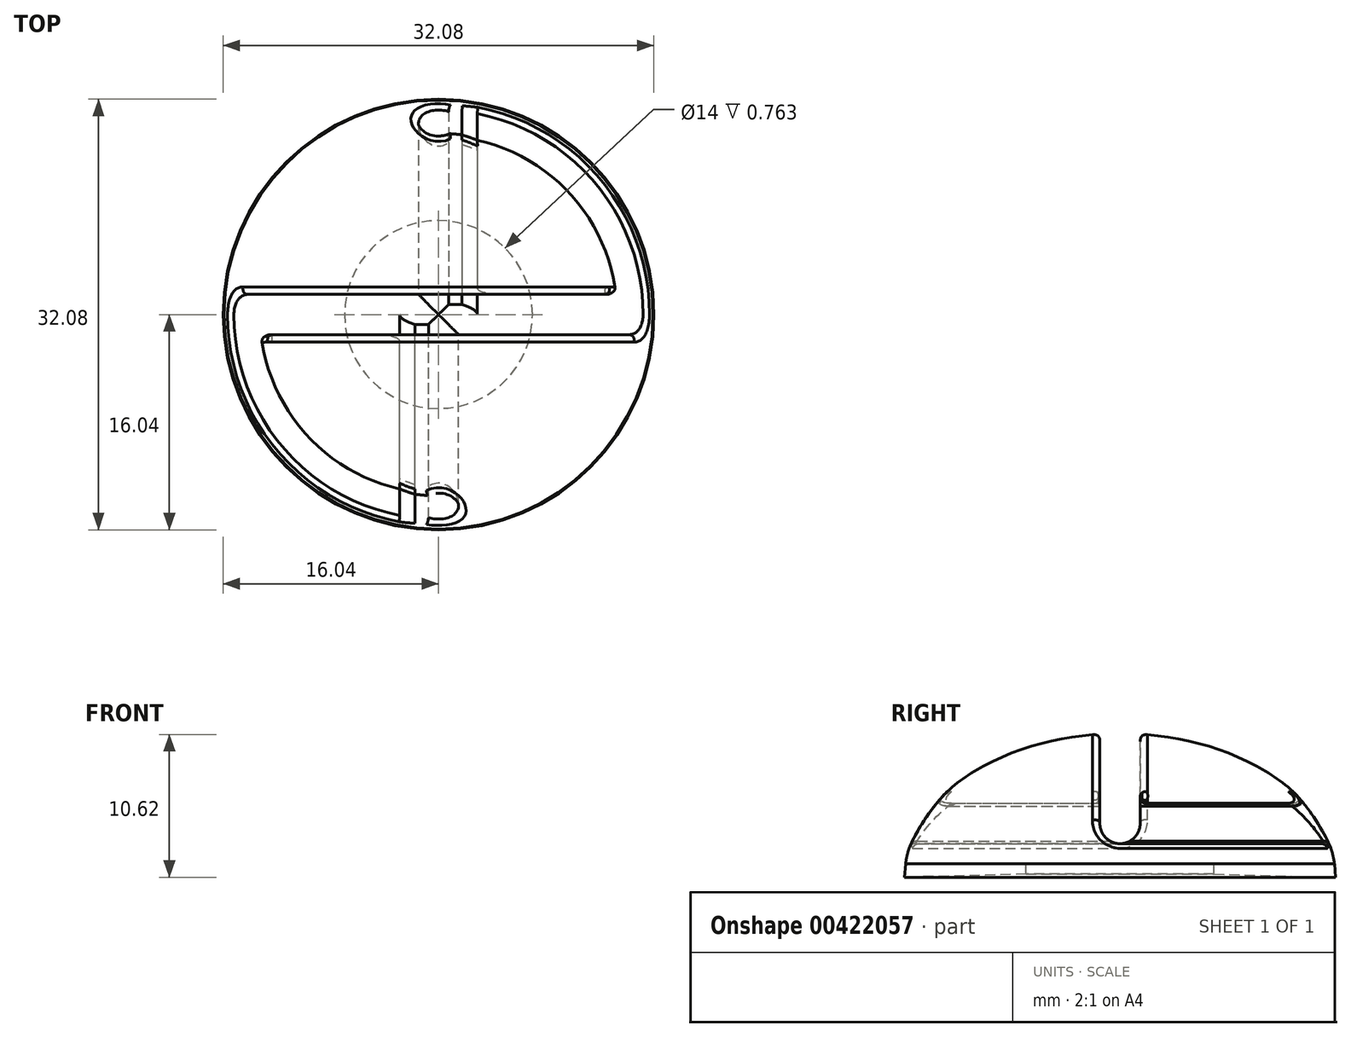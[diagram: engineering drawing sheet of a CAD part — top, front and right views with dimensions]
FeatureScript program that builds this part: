
annotation { "Feature Type Name" : "Feature", "Feature Type Description" : "" }
export const myFeature = defineFeature(function(context is Context, id is Id, definition is map)
    precondition{}
    {
        {
            var Q0;
            Q0=qCreatedBy(makeId("Front.planeOp"),FACE);
            var sketch = newSketch(context, id + "F0", { "sketchPlane" : qUnion([Q0])});
            skLineSegment(sketch, "E0", {"start": v(-7, 1) * mm, "end": v(0, 1) * mm});
            skLineSegment(sketch, "E1", {"start": v(0, 10.7) * mm, "end": v(0, 1) * mm});
            skPoint(sketch, "E2.orphan", {"position": v(0, 0) * mm});
            skLineSegment(sketch, "E3", {"start": v(-16.04, 0) * mm, "end": v(-7, 0.24) * mm});
            skLineSegment(sketch, "E4", {"start": v(-7, 0.24) * mm, "end": v(-7, 1) * mm});
            skLineSegment(sketch, "E5", {"start": v(-16.04, 0) * mm, "end": v(-15.97, 1) * mm});
            skEllipticalArc(sketch, "E6", {});
            const initialGuessF0  = {"E6": [0, 0, -1, 0, 0.016039070369298754, 0.010707691429102191, 4.71238898038469, 6.189886694139459]};
            skSetInitialGuess(sketch, initialGuessF0);
            skSolve(sketch);
        }
        {
            var Q0;
            Q0=makeQuery(id+"F0.imprint","IMPRINT",FACE,{"disambiguationData":[TD([[makeQuery(id+"F0.imprint","IMPRINT",EDGE,{"derivedFrom":sQuery(id+"F0.wireOp",EDGE,"E0")}),1.0]])]});
            var Q1;
            Q1=sQuery(id+"F0.wireOp",EDGE,"E1");
            revolve(context, id + "F1", {"entities" : qUnion([Q0]), "axis" : qUnion([Q1]), "revolveType" : RevolveType.FULL});
        }
        {
            var Q0;
            Q0=qCreatedBy(makeId("Right.planeOp"),FACE);
            var sketch = newSketch(context, id + "F2", { "sketchPlane" : qUnion([Q0])});
            skArc(sketch, "E7", {"start": v(-1.5, 4) * mm, "mid": v(0, 2.5) * mm, "end": v(1.5, 4) * mm});
            skLineSegment(sketch, "E8.top", {"start": v(-1.5, 10.74) * mm, "end": v(1.5, 10.74) * mm});
            skLineSegment(sketch, "E8.left", {"start": v(-1.5, 4) * mm, "end": v(-1.5, 10.74) * mm});
            skLineSegment(sketch, "E8.right", {"start": v(1.5, 4) * mm, "end": v(1.5, 10.74) * mm});
            skLineSegment(sketch, "E9", {"start": v(0, -1.52) * mm, "end": v(0, 4) * mm, "construction": true});
            skSolve(sketch);
        }
        {
            var Q0;
            Q0 = qSketchRegion(id + "F2", true);
            extrude(context, id + "F3", {"entities" : qUnion([Q0]), "operationType" : NewBodyOperationType.REMOVE, "endBound" : BoundingType.THROUGH_ALL, "oppositeDirection" : true, "depth" : 25 * mm, "hasSecondDirection" : true, "secondDirectionOppositeDirection" : false, "secondDirectionDepth" : 25 * mm});
        }
        {
            var Q0;
            Q0=qCreatedBy(makeId("Front.planeOp"),FACE);
            var sketch = newSketch(context, id + "F4", { "sketchPlane" : qUnion([Q0])});
            skLineSegment(sketch, "E10.bottom", {"start": v(0.75, 2.7) * mm, "end": v(1.75, 2.7) * mm});
            skLineSegment(sketch, "E10.top", {"start": v(0.75, 5.3) * mm, "end": v(1.75, 5.3) * mm});
            skArc(sketch, "E11", {"start": v(0.75, 5.3) * mm, "mid": v(-1.5, 4) * mm, "end": v(0.75, 2.7) * mm});
            skLineSegment(sketch, "E12", {"start": v(-2.06, 4) * mm, "end": v(6.5, 4) * mm, "construction": true});
            skLineSegment(sketch, "E13.bottom", {"start": v(2.88, 5.5) * mm, "end": v(16.29, 5.5) * mm});
            skLineSegment(sketch, "E13.top", {"start": v(2.88, 2.5) * mm, "end": v(16.29, 2.5) * mm});
            skLineSegment(sketch, "E13.right", {"start": v(16.29, 5.5) * mm, "end": v(16.29, 2.5) * mm});
            skLineSegment(sketch, "E14", {"start": v(2.88, 5.5) * mm, "end": v(1.75, 5.3) * mm});
            skLineSegment(sketch, "E15", {"start": v(2.88, 2.5) * mm, "end": v(1.75, 2.7) * mm});
            skSolve(sketch);
        }
        {
            var Q0;
            Q0=makeQuery(id+"F4.imprint","IMPRINT",FACE,{"disambiguationData":[TD([[makeQuery(id+"F4.imprint","IMPRINT",EDGE,{"derivedFrom":sQuery(id+"F4.wireOp",EDGE,"E10.bottom")}),1.0]])]});
            extrude(context, id + "F5", {"entities" : qUnion([Q0]), "operationType" : NewBodyOperationType.REMOVE, "endBound" : BoundingType.THROUGH_ALL, "oppositeDirection" : true, "depth" : 25 * mm});
        }
        {
            var Q0;
            Q0=qCreatedBy(makeId("Front.planeOp"),FACE);
            var sketch = newSketch(context, id + "F6", { "sketchPlane" : qUnion([Q0])});
            skLineSegment(sketch, "E16.bottom", {"start": v(-0.75, 5.3) * mm, "end": v(-1.75, 5.3) * mm});
            skLineSegment(sketch, "E16.top", {"start": v(-0.75, 2.7) * mm, "end": v(-1.75, 2.7) * mm});
            skArc(sketch, "E17", {"start": v(-0.75, 2.7) * mm, "mid": v(1.5, 4) * mm, "end": v(-0.75, 5.3) * mm});
            skLineSegment(sketch, "E18", {"start": v(-13.28, 4) * mm, "end": v(-21.85, 4) * mm, "construction": true});
            skLineSegment(sketch, "E19.bottom", {"start": v(-2.88, 2.5) * mm, "end": v(-16.07, 2.5) * mm});
            skLineSegment(sketch, "E19.top", {"start": v(-2.88, 5.5) * mm, "end": v(-16.07, 5.5) * mm});
            skLineSegment(sketch, "E19.right", {"start": v(-16.07, 2.5) * mm, "end": v(-16.07, 5.5) * mm});
            skLineSegment(sketch, "E20", {"start": v(-2.88, 2.5) * mm, "end": v(-1.75, 2.7) * mm});
            skLineSegment(sketch, "E21", {"start": v(-2.88, 5.5) * mm, "end": v(-1.75, 5.3) * mm});
            skLineSegment(sketch, "E22", {"start": v(0, -1.12) * mm, "end": v(0, 10.48) * mm, "construction": true});
            skSolve(sketch);
        }
        {
            var Q0;
            Q0 = qSketchRegion(id + "F6", true);
            extrude(context, id + "F7", {"entities" : qUnion([Q0]), "operationType" : NewBodyOperationType.REMOVE, "endBound" : BoundingType.THROUGH_ALL, "depth" : 25 * mm});
        }
        {
            var Q0;
            Q0=makeQuery(id+"F3.boolean.opBoolean","INTERSECT",EDGE,{"derivedFrom":[makeQuery(id+"F1.opRevolve","SWEPT_FACE",FACE,{"disambiguationData":[OSD([sQuery(id+"F0.wireOp",EDGE,"E6")])]}),makeQuery(id+"F3.opExtrude","SWEPT_FACE",FACE,{"disambiguationData":[OSD([sQuery(id+"F2.wireOp",EDGE,"E8.left")])]})]});
            var Q1;
            Q1=makeQuery(id+"F7.boolean.opBoolean","INTERSECT",EDGE,{"derivedFrom":[makeQuery(id+"F1.opRevolve","SWEPT_FACE",FACE,{"disambiguationData":[OSD([sQuery(id+"F0.wireOp",EDGE,"E6")])]}),makeQuery(id+"F7.opExtrude","SWEPT_FACE",FACE,{"disambiguationData":[OSD([sQuery(id+"F6.wireOp",EDGE,"E19.top")])]})]});
            var Q2;
            Q2=makeQuery(id+"F7.boolean.opBoolean","INTERSECT",EDGE,{"derivedFrom":[makeQuery(id+"F3.boolean.opBoolean","COPY",FACE,{"derivedFrom":makeQuery(id+"F3.opExtrude","SWEPT_FACE",FACE,{"disambiguationData":[OSD([sQuery(id+"F2.wireOp",EDGE,"E8.left")])]})}),makeQuery(id+"F7.opExtrude","SWEPT_FACE",FACE,{"disambiguationData":[OSD([sQuery(id+"F6.wireOp",EDGE,"E19.top")])]})]});
            var Q3;
            Q3=makeQuery(id+"F7.boolean.opBoolean","INTERSECT",EDGE,{"derivedFrom":[makeQuery(id+"F1.opRevolve","SWEPT_FACE",FACE,{"disambiguationData":[OSD([sQuery(id+"F0.wireOp",EDGE,"E6")])]}),makeQuery(id+"F7.opExtrude","SWEPT_FACE",FACE,{"disambiguationData":[OSD([sQuery(id+"F6.wireOp",EDGE,"E16.bottom")])]})]});
            var Q4;
            Q4=makeQuery(id+"F7.boolean.opBoolean","INTERSECT",EDGE,{"derivedFrom":[makeQuery(id+"F1.opRevolve","SWEPT_FACE",FACE,{"disambiguationData":[OSD([sQuery(id+"F0.wireOp",EDGE,"E6")])]}),makeQuery(id+"F7.opExtrude","SWEPT_FACE",FACE,{"disambiguationData":[OSD([sQuery(id+"F6.wireOp",EDGE,"E21")])]})]});
            var Q5;
            Q5=makeQuery(id+"F7.boolean.opBoolean","INTERSECT",EDGE,{"derivedFrom":[makeQuery(id+"F1.opRevolve","SWEPT_FACE",FACE,{"disambiguationData":[OSD([sQuery(id+"F0.wireOp",EDGE,"E6")])]}),makeQuery(id+"F7.opExtrude","SWEPT_FACE",FACE,{"disambiguationData":[OSD([sQuery(id+"F6.wireOp",EDGE,"E17")])]})]});
            var Q6;
            Q6=makeQuery(id+"F7.boolean.opBoolean","INTERSECT",EDGE,{"derivedFrom":[makeQuery(id+"F1.opRevolve","SWEPT_FACE",FACE,{"disambiguationData":[OSD([sQuery(id+"F0.wireOp",EDGE,"E6")])]}),makeQuery(id+"F7.opExtrude","SWEPT_FACE",FACE,{"disambiguationData":[OSD([sQuery(id+"F6.wireOp",EDGE,"E16.top")])]})]});
            var Q7;
            Q7=makeQuery(id+"F7.boolean.opBoolean","INTERSECT",EDGE,{"derivedFrom":[makeQuery(id+"F1.opRevolve","SWEPT_FACE",FACE,{"disambiguationData":[OSD([sQuery(id+"F0.wireOp",EDGE,"E6")])]}),makeQuery(id+"F7.opExtrude","SWEPT_FACE",FACE,{"disambiguationData":[OSD([sQuery(id+"F6.wireOp",EDGE,"E20")])]})]});
            var Q8;
            Q8=makeQuery(id+"F7.boolean.opBoolean","INTERSECT",EDGE,{"derivedFrom":[makeQuery(id+"F1.opRevolve","SWEPT_FACE",FACE,{"disambiguationData":[OSD([sQuery(id+"F0.wireOp",EDGE,"E6")])]}),makeQuery(id+"F7.opExtrude","SWEPT_FACE",FACE,{"disambiguationData":[OSD([sQuery(id+"F6.wireOp",EDGE,"E19.bottom")])]})]});
            var Q9;
            Q9=makeQuery(id+"F5.boolean.opBoolean","INTERSECT",EDGE,{"derivedFrom":[makeQuery(id+"F1.opRevolve","SWEPT_FACE",FACE,{"disambiguationData":[OSD([sQuery(id+"F0.wireOp",EDGE,"E6")])]}),makeQuery(id+"F5.opExtrude","SWEPT_FACE",FACE,{"disambiguationData":[OSD([sQuery(id+"F4.wireOp",EDGE,"E13.bottom")])]})]});
            var Q10;
            Q10=makeQuery(id+"F5.boolean.opBoolean","INTERSECT",EDGE,{"derivedFrom":[makeQuery(id+"F1.opRevolve","SWEPT_FACE",FACE,{"disambiguationData":[OSD([sQuery(id+"F0.wireOp",EDGE,"E6")])]}),makeQuery(id+"F5.opExtrude","SWEPT_FACE",FACE,{"disambiguationData":[OSD([sQuery(id+"F4.wireOp",EDGE,"E14")])]})]});
            var Q11;
            Q11=makeQuery(id+"F5.boolean.opBoolean","INTERSECT",EDGE,{"derivedFrom":[makeQuery(id+"F1.opRevolve","SWEPT_FACE",FACE,{"disambiguationData":[OSD([sQuery(id+"F0.wireOp",EDGE,"E6")])]}),makeQuery(id+"F5.opExtrude","SWEPT_FACE",FACE,{"disambiguationData":[OSD([sQuery(id+"F4.wireOp",EDGE,"E10.top")])]})]});
            var Q12;
            Q12=makeQuery(id+"F5.boolean.opBoolean","INTERSECT",EDGE,{"derivedFrom":[makeQuery(id+"F1.opRevolve","SWEPT_FACE",FACE,{"disambiguationData":[OSD([sQuery(id+"F0.wireOp",EDGE,"E6")])]}),makeQuery(id+"F5.opExtrude","SWEPT_FACE",FACE,{"disambiguationData":[OSD([sQuery(id+"F4.wireOp",EDGE,"E11")])]})]});
            var Q13;
            Q13=makeQuery(id+"F5.boolean.opBoolean","INTERSECT",EDGE,{"derivedFrom":[makeQuery(id+"F1.opRevolve","SWEPT_FACE",FACE,{"disambiguationData":[OSD([sQuery(id+"F0.wireOp",EDGE,"E6")])]}),makeQuery(id+"F5.opExtrude","SWEPT_FACE",FACE,{"disambiguationData":[OSD([sQuery(id+"F4.wireOp",EDGE,"E10.bottom")])]})]});
            var Q14;
            Q14=makeQuery(id+"F5.boolean.opBoolean","INTERSECT",EDGE,{"derivedFrom":[makeQuery(id+"F1.opRevolve","SWEPT_FACE",FACE,{"disambiguationData":[OSD([sQuery(id+"F0.wireOp",EDGE,"E6")])]}),makeQuery(id+"F5.opExtrude","SWEPT_FACE",FACE,{"disambiguationData":[OSD([sQuery(id+"F4.wireOp",EDGE,"E15")])]})]});
            var Q15;
            Q15=makeQuery(id+"F5.boolean.opBoolean","INTERSECT",EDGE,{"derivedFrom":[makeQuery(id+"F3.boolean.opBoolean","COPY",FACE,{"derivedFrom":makeQuery(id+"F3.opExtrude","SWEPT_FACE",FACE,{"disambiguationData":[OSD([sQuery(id+"F2.wireOp",EDGE,"E8.right")])]})}),makeQuery(id+"F5.opExtrude","SWEPT_FACE",FACE,{"disambiguationData":[OSD([sQuery(id+"F4.wireOp",EDGE,"E13.bottom")])]})]});
            fillet(context, id + "F8", {"entities" : qUnion([Q0, Q1, Q2, Q3, Q4, Q5, Q6, Q7, Q8, Q9, Q10, Q11, Q12, Q13, Q14, Q15]), "radius" : 0.5 * mm, "tangentPropagation" : true, "rho" : 0.5, "crossSection" : FilletCrossSection.CONIC, "allowEdgeOverflow" : false});
        }
    });
